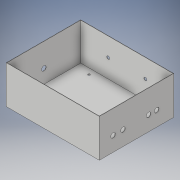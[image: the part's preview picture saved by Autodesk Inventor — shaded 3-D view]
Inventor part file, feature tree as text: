
AUTODESK INVENTOR PART (.ipt)
format: ipt  version: 2018 (Build 220112000, 112)  size: 156,672 bytes
history: native  units: in
note: dims shown in document units (in); Inventor stores cm internally (conversion verified against a paired STEP export)
features: extrude x6, sketch x6
ambient origin geometry x8: Origin, YZ Plane, XZ Plane, XY Plane, X Axis, Y Axis, Z Axis, Center Point
bodies: Solid1 (feature_tree)
feature tree (12):
  extrude  "Extrusion1"  Depth=4.0in
  extrude  "Extrusion2"  Depth=4.96in
  extrude  "Extrusion3"  Depth=2.0in TaperAngle=0.0deg
  extrude  "Extrusion4"  Depth=0.164in
  extrude  "Extrusion5"  Depth=3.937in
  extrude  "Extrusion6"  Depth=0.112in
  sketch  "Sketch1"  dims[d0=5.0in d1=4.0in]
  sketch  "Sketch2"  dims[d2=0.04in d3=0.0in d4=4.96in]
  sketch  "Sketch3"  dims[d5=3.96in d6=2.0in d7=0.0in]
  sketch  "Sketch4"  dims[d10=0.164in d12=0.164in]
  sketch  "Sketch5"  dims[d13=0.0in d14=0.0in d15=3.937in]
  sketch  "Sketch6"  dims[d16=3.937in d23=0.112in d24=0.112in d25=0.112in d26=0.0in d27=0.0in d28=0.25in d29=0.112in d30=0.0in d31=0.115in d32=0.0in d33=0.781in d34=0.438in d35=0.0in d36=1.375in d37=0.0in d38=0.532in d39=0.0in d40=0.25in d41=0.25in d42=0.25in d43=0.25in d44=0.0in d45=0.0in]
